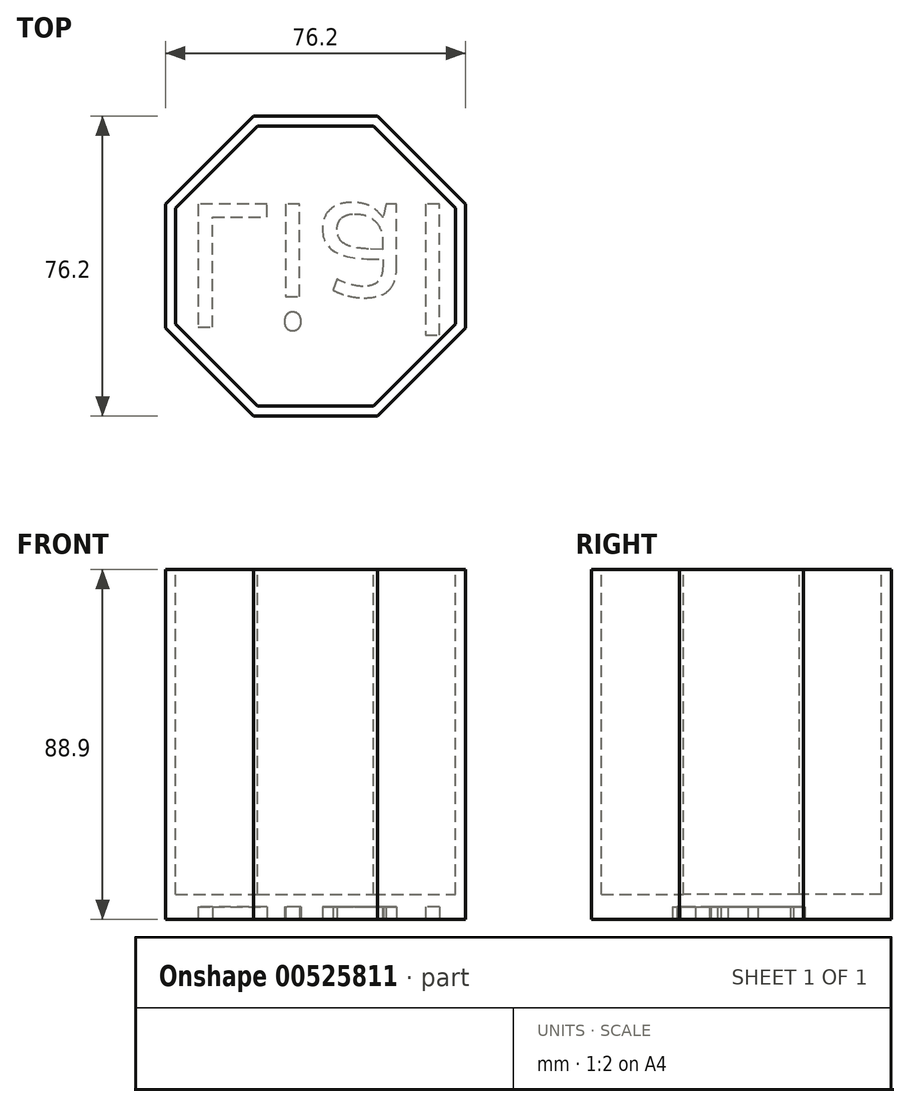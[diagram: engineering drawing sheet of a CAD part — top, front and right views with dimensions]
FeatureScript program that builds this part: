
annotation { "Feature Type Name" : "Feature", "Feature Type Description" : "" }
export const myFeature = defineFeature(function(context is Context, id is Id, definition is map)
    precondition{}
    {
        {
            var Q0;
            Q0=qCreatedBy(makeId("Top.planeOp"),FACE);
            var sketch = newSketch(context, id + "F0", { "sketchPlane" : qUnion([Q0])});
            skCircle(sketch, "E0.cCircle", {"center": v(0, 0) * mm, "radius": 38.1 * mm, "construction": true});
            skLineSegment(sketch, "E0.0", {"start": v(38.1, 15.78) * mm, "end": v(38.1, -15.78) * mm});
            skLineSegment(sketch, "E0.1", {"start": v(38.1, -15.78) * mm, "end": v(15.78, -38.1) * mm});
            skLineSegment(sketch, "E0.2", {"start": v(15.78, -38.1) * mm, "end": v(-15.78, -38.1) * mm});
            skLineSegment(sketch, "E0.3", {"start": v(-15.78, -38.1) * mm, "end": v(-38.1, -15.78) * mm});
            skLineSegment(sketch, "E0.4", {"start": v(-38.1, -15.78) * mm, "end": v(-38.1, 15.78) * mm});
            skLineSegment(sketch, "E0.5", {"start": v(-38.1, 15.78) * mm, "end": v(-15.78, 38.1) * mm});
            skLineSegment(sketch, "E0.6", {"start": v(-15.78, 38.1) * mm, "end": v(15.78, 38.1) * mm});
            skLineSegment(sketch, "E0.7", {"start": v(15.78, 38.1) * mm, "end": v(38.1, 15.78) * mm});
            skPoint(sketch, "E0.0.midPoint", {"position": v(38.1, 0) * mm});
            skSolve(sketch);
        }
        {
            var Q0;
            Q0=makeQuery(id+"F0.imprint","IMPRINT",FACE,{"disambiguationData":[TD([[makeQuery(id+"F0.imprint","IMPRINT",EDGE,{"derivedFrom":sQuery(id+"F0.wireOp",EDGE,"E0.0")}),-1.0]])]});
            extrude(context, id + "F1", {"entities" : qUnion([Q0]), "depth" : 88.9 * mm, "offsetDistance" : 25.4 * mm});
        }
        {
            var Q0;
            Q0=makeQuery(id+"F1.opExtrude","CAP_FACE",FACE,{"disambiguationData":[OSD([sQuery(id+"F0.wireOp",EDGE,"E0.0"),sQuery(id+"F0.wireOp",EDGE,"E0.1"),sQuery(id+"F0.wireOp",EDGE,"E0.2"),sQuery(id+"F0.wireOp",EDGE,"E0.3"),sQuery(id+"F0.wireOp",EDGE,"E0.4"),sQuery(id+"F0.wireOp",EDGE,"E0.5"),sQuery(id+"F0.wireOp",EDGE,"E0.6"),sQuery(id+"F0.wireOp",EDGE,"E0.7")])],"isStart":false});
            var sketch = newSketch(context, id + "F2", { "sketchPlane" : qUnion([Q0])});
            skCircle(sketch, "E1.cCircle", {"center": v(0, 0) * mm, "radius": 35.56 * mm, "construction": true});
            skLineSegment(sketch, "E1.0", {"start": v(35.56, 14.73) * mm, "end": v(35.56, -14.73) * mm});
            skLineSegment(sketch, "E1.1", {"start": v(35.56, -14.73) * mm, "end": v(14.73, -35.56) * mm});
            skLineSegment(sketch, "E1.2", {"start": v(14.73, -35.56) * mm, "end": v(-14.73, -35.56) * mm});
            skLineSegment(sketch, "E1.3", {"start": v(-14.73, -35.56) * mm, "end": v(-35.56, -14.73) * mm});
            skLineSegment(sketch, "E1.4", {"start": v(-35.56, -14.73) * mm, "end": v(-35.56, 14.73) * mm});
            skLineSegment(sketch, "E1.5", {"start": v(-35.56, 14.73) * mm, "end": v(-14.73, 35.56) * mm});
            skLineSegment(sketch, "E1.6", {"start": v(-14.73, 35.56) * mm, "end": v(14.73, 35.56) * mm});
            skLineSegment(sketch, "E1.7", {"start": v(14.73, 35.56) * mm, "end": v(35.56, 14.73) * mm});
            skPoint(sketch, "E1.0.midPoint", {"position": v(35.56, 0) * mm});
            skSolve(sketch);
        }
        {
            var Q0;
            Q0=makeQuery(id+"F2.imprint","IMPRINT",FACE,{"disambiguationData":[TD([[makeQuery(id+"F2.imprint","IMPRINT",EDGE,{"derivedFrom":sQuery(id+"F2.wireOp",EDGE,"E1.0")}),-1.0]])]});
            extrude(context, id + "F3", {"entities" : qUnion([Q0]), "operationType" : NewBodyOperationType.REMOVE, "oppositeDirection" : true, "depth" : 82.55 * mm, "offsetDistance" : 25.4 * mm});
        }
        {
            var Q0;
            Q0=makeQuery(id+"F1.opExtrude","CAP_FACE",FACE,{"disambiguationData":[OSD([sQuery(id+"F0.wireOp",EDGE,"E0.0"),sQuery(id+"F0.wireOp",EDGE,"E0.1"),sQuery(id+"F0.wireOp",EDGE,"E0.2"),sQuery(id+"F0.wireOp",EDGE,"E0.3"),sQuery(id+"F0.wireOp",EDGE,"E0.4"),sQuery(id+"F0.wireOp",EDGE,"E0.5"),sQuery(id+"F0.wireOp",EDGE,"E0.6"),sQuery(id+"F0.wireOp",EDGE,"E0.7")])],"isStart":true});
            var sketch = newSketch(context, id + "F4", { "sketchPlane" : qUnion([Q0])});
            skText(sketch, "E2", { "text": "Lial", "fontName": "OpenSans-Regular.ttf"});
            const initialGuessF4  = {"E2": [-0.0341, -0.01575, 1, 0, 0.03156]};
            skSetInitialGuess(sketch, initialGuessF4);
            skSolve(sketch);
        }
        {
            var Q0;
            Q0 = qSketchRegion(id + "F4", true);
            extrude(context, id + "F5", {"entities" : qUnion([Q0]), "operationType" : NewBodyOperationType.REMOVE, "oppositeDirection" : true, "depth" : 3.17 * mm, "offsetDistance" : 25.4 * mm});
        }
    });
